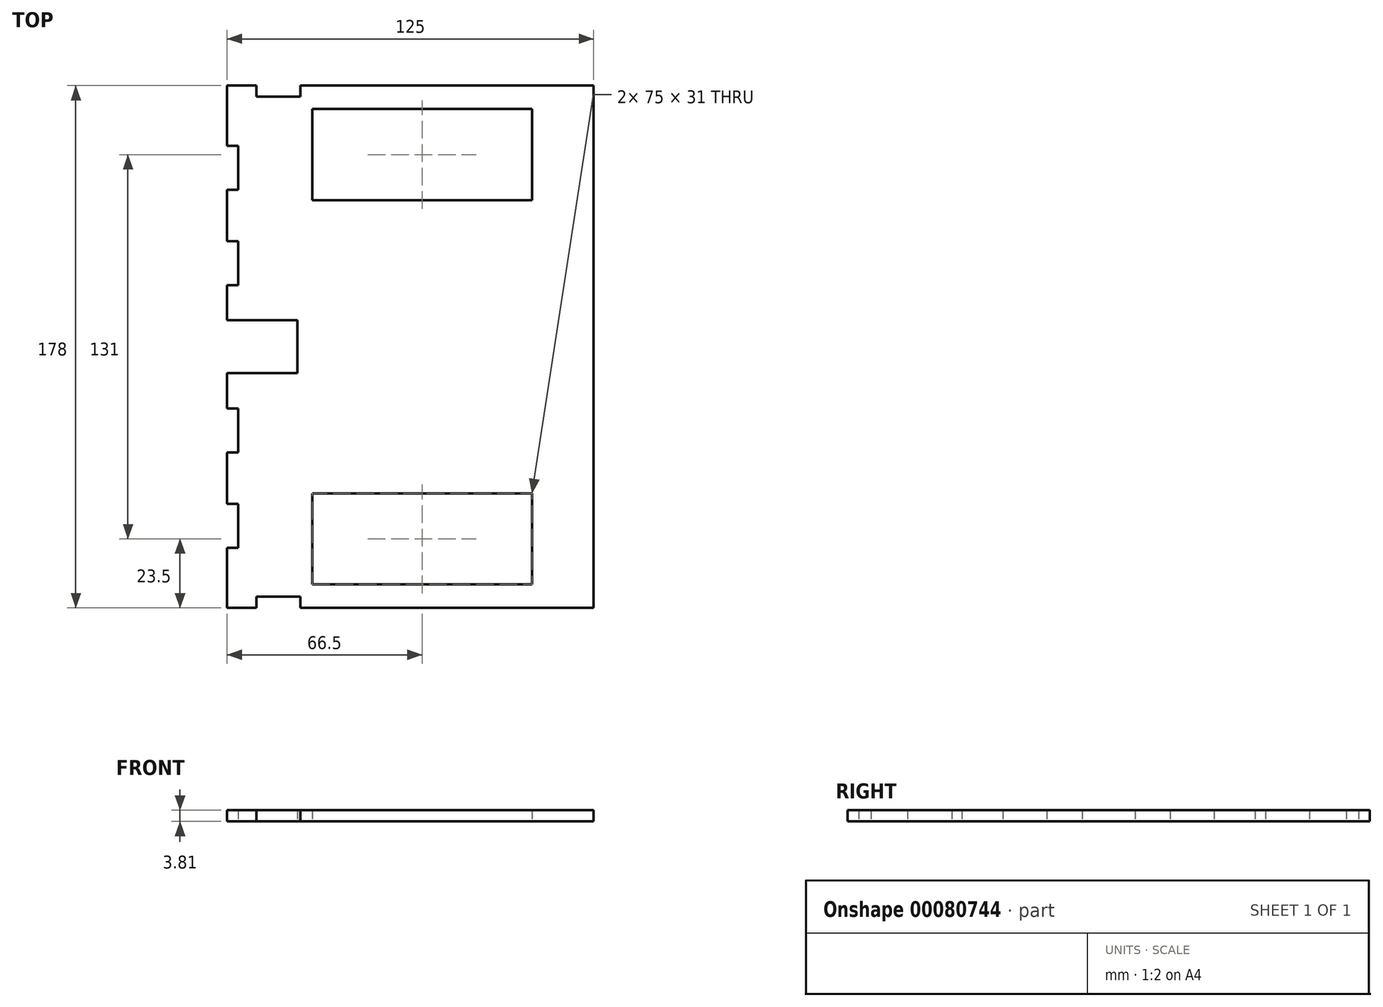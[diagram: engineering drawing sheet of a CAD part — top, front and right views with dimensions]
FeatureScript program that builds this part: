
annotation { "Feature Type Name" : "Feature", "Feature Type Description" : "" }
export const myFeature = defineFeature(function(context is Context, id is Id, definition is map)
    precondition{}
    {
        {
            var Q0;
            Q0=qCreatedBy(makeId("Top.planeOp"),FACE);
            var sketch = newSketch(context, id + "F0", { "sketchPlane" : qUnion([Q0])});
            skLineSegment(sketch, "E0.bottom", {"start": v(62.5, 89) * mm, "end": v(-62.5, 89) * mm});
            skLineSegment(sketch, "E0.top", {"start": v(62.5, -89) * mm, "end": v(-62.5, -89) * mm});
            skLineSegment(sketch, "E0.left", {"start": v(62.5, 89) * mm, "end": v(62.5, -89) * mm});
            skLineSegment(sketch, "E0.right", {"start": v(-62.5, 89) * mm, "end": v(-62.5, -89) * mm});
            skPoint(sketch, "E0.middle", {"position": v(0, 0) * mm});
            skLineSegment(sketch, "E1.bottom", {"start": v(41.5, 81) * mm, "end": v(-33.5, 81) * mm});
            skLineSegment(sketch, "E1.top", {"start": v(41.5, 50) * mm, "end": v(-33.5, 50) * mm});
            skLineSegment(sketch, "E1.left", {"start": v(41.5, 81) * mm, "end": v(41.5, 50) * mm});
            skLineSegment(sketch, "E1.right", {"start": v(-33.5, 81) * mm, "end": v(-33.5, 50) * mm});
            skPoint(sketch, "E1.middle", {"position": v(4, 65.5) * mm});
            skLineSegment(sketch, "E2", {"start": v(-62.5, 0) * mm, "end": v(62.5, 0) * mm, "construction": true});
            skLineSegment(sketch, "E3.MirrorCS", {"start": v(-33.5, -81) * mm, "end": v(-33.5, -50) * mm});
            skLineSegment(sketch, "E4.MirrorCS", {"start": v(41.5, -81) * mm, "end": v(-33.5, -81) * mm});
            skLineSegment(sketch, "E5.MirrorCS", {"start": v(41.5, -81) * mm, "end": v(41.5, -50) * mm});
            skLineSegment(sketch, "E6.MirrorCS", {"start": v(41.5, -50) * mm, "end": v(-33.5, -50) * mm});
            skLineSegment(sketch, "E7", {"start": v(-62.5, 9) * mm, "end": v(-38.5, 9) * mm});
            skLineSegment(sketch, "E8", {"start": v(-38.5, 9) * mm, "end": v(-38.5, 0) * mm});
            skLineSegment(sketch, "E9.MirrorCS", {"start": v(-38.5, -9) * mm, "end": v(-38.5, 0) * mm});
            skLineSegment(sketch, "E10.MirrorCS", {"start": v(-62.5, -9) * mm, "end": v(-38.5, -9) * mm});
            skLineSegment(sketch, "E11", {"start": v(-52.5, -89) * mm, "end": v(-52.5, -85.19) * mm});
            skLineSegment(sketch, "E12", {"start": v(-52.5, -85.19) * mm, "end": v(-37.5, -85.19) * mm});
            skLineSegment(sketch, "E13", {"start": v(-37.5, -85.19) * mm, "end": v(-37.5, -89) * mm});
            skLineSegment(sketch, "E14.MirrorCS", {"start": v(-52.5, 85.19) * mm, "end": v(-37.5, 85.19) * mm});
            skLineSegment(sketch, "E15.MirrorCS", {"start": v(-52.5, 89) * mm, "end": v(-52.5, 85.19) * mm});
            skLineSegment(sketch, "E16.MirrorCS", {"start": v(-37.5, 85.19) * mm, "end": v(-37.5, 89) * mm});
            skLineSegment(sketch, "E17", {"start": v(62.5, 79) * mm, "end": v(58.69, 79) * mm});
            skLineSegment(sketch, "E18", {"start": v(58.69, 79) * mm, "end": v(58.69, 64) * mm});
            skLineSegment(sketch, "E19", {"start": v(58.69, 64) * mm, "end": v(62.5, 64) * mm});
            skLineSegment(sketch, "E20", {"start": v(62.5, 54) * mm, "end": v(58.69, 54) * mm});
            skLineSegment(sketch, "E21", {"start": v(58.69, 54) * mm, "end": v(58.69, 39) * mm});
            skLineSegment(sketch, "E22", {"start": v(58.7, 39) * mm, "end": v(62.5, 39) * mm});
            skLineSegment(sketch, "E23.MirrorCS", {"start": v(58.7, -39) * mm, "end": v(62.5, -39) * mm});
            skLineSegment(sketch, "E24.MirrorCS", {"start": v(58.7, -54) * mm, "end": v(58.7, -39) * mm});
            skLineSegment(sketch, "E25.MirrorCS", {"start": v(62.5, -54) * mm, "end": v(58.69, -54) * mm});
            skLineSegment(sketch, "E26.MirrorCS", {"start": v(58.69, -64) * mm, "end": v(62.5, -64) * mm});
            skLineSegment(sketch, "E27.MirrorCS", {"start": v(58.7, -79) * mm, "end": v(58.7, -64) * mm});
            skLineSegment(sketch, "E28.MirrorCS", {"start": v(62.5, -79) * mm, "end": v(58.69, -79) * mm});
            skLineSegment(sketch, "E29", {"start": v(-62.5, 68.5) * mm, "end": v(-58.69, 68.5) * mm});
            skLineSegment(sketch, "E30", {"start": v(-58.7, 68.5) * mm, "end": v(-58.7, 53.5) * mm});
            skLineSegment(sketch, "E31", {"start": v(-58.69, 53.5) * mm, "end": v(-62.5, 53.5) * mm});
            skLineSegment(sketch, "E32", {"start": v(-62.5, 36) * mm, "end": v(-58.69, 36) * mm});
            skLineSegment(sketch, "E33", {"start": v(-58.7, 36) * mm, "end": v(-58.7, 21) * mm});
            skLineSegment(sketch, "E34", {"start": v(-58.69, 21) * mm, "end": v(-62.5, 21) * mm});
            skLineSegment(sketch, "E35.MirrorCS", {"start": v(-58.69, -36) * mm, "end": v(-58.69, -21) * mm});
            skLineSegment(sketch, "E36.MirrorCS", {"start": v(-58.69, -21) * mm, "end": v(-62.5, -21) * mm});
            skLineSegment(sketch, "E37.MirrorCS", {"start": v(-62.5, -36) * mm, "end": v(-58.69, -36) * mm});
            skLineSegment(sketch, "E38.MirrorCS", {"start": v(-58.69, -53.5) * mm, "end": v(-62.5, -53.5) * mm});
            skLineSegment(sketch, "E39.MirrorCS", {"start": v(-58.7, -68.5) * mm, "end": v(-58.7, -53.5) * mm});
            skLineSegment(sketch, "E40.MirrorCS", {"start": v(-62.5, -68.5) * mm, "end": v(-58.69, -68.5) * mm});
            skSolve(sketch);
        }
        {
            var Q0;
            Q0=makeQuery(id+"F0.imprint","IMPRINT",FACE,{"disambiguationData":[TD([[makeQuery(id+"F0.imprint","IMPRINT",EDGE,{"derivedFrom":sQuery(id+"F0.wireOp",EDGE,"E0.bottom")}),1.0]])]});
            var Q1;
            {var subQ0=sQuery(id+"F0.wireOp",EDGE,"E26.MirrorCS");Q1=makeQuery(id+"F0.imprint","IMPRINT",FACE,{"disambiguationData":[TD([[makeQuery(id+"F0.imprint","IMPRINT",EDGE,{"derivedFrom":subQ0}),-1.0]])]});}
            var Q2;
            {var subQ0=sQuery(id+"F0.wireOp",EDGE,"E23.MirrorCS");Q2=makeQuery(id+"F0.imprint","IMPRINT",FACE,{"disambiguationData":[TD([[makeQuery(id+"F0.imprint","IMPRINT",EDGE,{"derivedFrom":subQ0}),-1.0]])]});}
            var Q3;
            {var subQ0=sQuery(id+"F0.wireOp",EDGE,"E20");Q3=makeQuery(id+"F0.imprint","IMPRINT",FACE,{"disambiguationData":[TD([[makeQuery(id+"F0.imprint","IMPRINT",EDGE,{"derivedFrom":subQ0}),1.0]])]});}
            var Q4;
            {var subQ0=sQuery(id+"F0.wireOp",EDGE,"E17");Q4=makeQuery(id+"F0.imprint","IMPRINT",FACE,{"disambiguationData":[TD([[makeQuery(id+"F0.imprint","IMPRINT",EDGE,{"derivedFrom":subQ0}),1.0]])]});}
            extrude(context, id + "F1", {"entities" : qUnion([Q0, Q1, Q2, Q3, Q4]), "depth" : 3.8 * mm});
        }
    });
